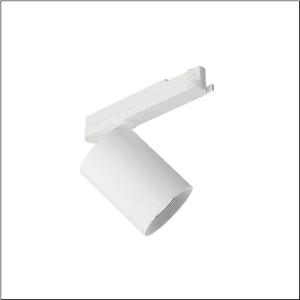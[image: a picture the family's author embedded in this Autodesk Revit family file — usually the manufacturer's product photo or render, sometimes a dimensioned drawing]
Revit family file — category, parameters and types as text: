
# Revit family: spot_21_51se13dbd5b
name_source: partatom
category: Lighting Fixtures
units: mm (PartAtom-declared; Revit-internal decimal feet)

## family parameters
Cut with Voids When Loaded = No
Host = Face
Light Source = No
Part Type = Normal
Room Calculation Point = No
Round Connector Dimension = Use Diameter
Shared = No

## types (1)
- --- (1 x LED, 5410 lm, 42.1 W, 4000K)
    Apparent Load = 42 VA
    CIE Flux Codes = 95 98 99 100 100
    Color Rendering = 90
    Color Temperature = 4000K
    Default Elevation = 1800 mm
    Description = Spot 21, directional spotlight, light control with lens, of PMMA, LED rated luminous flux: 5.200lm, light colour: 940, control gear: ECG Multilumen, with 3-phase adapter, mains connection: 220..240V, AC, 50/60Hz, of aluminium, traffic white (RAL 9016), length: 253mm, diameter: 105mm, protection rating (complete): IP20, insulation class (complete): insulation class I (protective earthing), certification: CE, impact resistance: IK02, permissible ambient temperature for indoor applications: -20..+40°C, packaging unit: 1 piece
    Height = 175 mm
    Lamp = 1 x LED
    Lamp Light Flux = 5410 lm
    Lamp Power = 42.1 W
    Lamp count = 1
    Length = 105 mm
    Luminous efficacy = 129 lm/W
    Manufacturer = Siteco
    ModVariant = No
    Model = 51SE13DBD5B
    Mounting Place = Ceiling
    Mounting Type = Pendant
    Number of Poles = 1
    OnlyDefault = Yes
    Power Factor = 1
    Product Name = Spot 21
    Product group = directional spotlight
    ProductGroupID = 905
    Protection Class = Protection class I
    Protection Degree = IP 20
    RLX_Detail_Level = 1
    RLX_Emergency_Light_Flux = 0 lm
    RLX_Emergency_Type = 0
    RLX_Emergency_Type_DB = No
    RlxData = <blob elided: 17725 chars, md5=992841ed>
    Socket = socket
    Standby Power = 0 W
    System Light Flux = 5410 lm
    System Power = 42 W
    Type Comments = factory setting: luminous flux: 100 % | (ON | ON | ON | ON) | 1050 mA
    Type Image = l_1003976.jpg
    URL = http://relux.com
    VarID = @adj_093585
    Voltage = 0 V
    Weight = 0.00 kg
    Width = 0 mm  [stored 0 ft]

note: [stored X ft] marks values corroborated as IEEE doubles in the binary element streams (Revit-internal decimal feet)

## geometry (parser evidence)
native form markers: Blend x4, Sweep x10
no freeform markers — native parametric forms only
